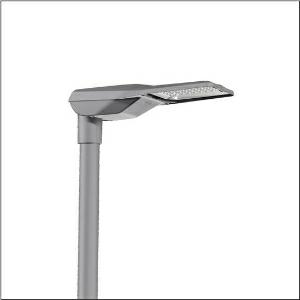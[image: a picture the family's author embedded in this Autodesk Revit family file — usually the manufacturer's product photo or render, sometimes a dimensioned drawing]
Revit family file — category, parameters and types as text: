
# Revit family: streetlight_sl_21_iq_mini___st0_5a_5xe2b41g08jb_20f7
name_source: partatom
category: Lighting Fixtures
units: mm (PartAtom-declared; Revit-internal decimal feet)

## family parameters
Cut with Voids When Loaded = No
Host = Face
Light Source = No
Part Type = Normal
Room Calculation Point = No
Round Connector Dimension = Use Diameter
Shared = No

## types (1)
- --- (1 x LED, 11290 lm, 71.6 W, 4000K)
    Apparent Load = 72 VA
    CIE Flux Codes = 43 76 97 100 100
    Color Rendering = 70
    Color Temperature = 4000K
    Default Elevation = 1800 mm
    Description = Streetlight SL 21 iQ mini, mast luminaire, primary light control with lens, of PMMA, primary optical cover: cover, of toughened safety glass, transparent, light distribution: ST0.5a, light emission: direct distribution, primary light characteristic: asymmetric, installation type: post-top, side-entry, LED, High Power LED, rated luminous flux: 11.290lm, luminous efficacy: 158lm/W, light colour: 740, colour temperature: 4000K, control gear: iQ Street-Remote, control: Street-Remote, Auto-Match, Temp-Guard, Lumen-Switch, Night-Set, Smart-Wire, Light-Fading, Desk-Remote (wireless, voltage-free reading and setting of iQ features in the workshop via application-optimized NFC function/RFID function), optimised constant luminous flux control (CLO 2.0), pre-setting: linear dimming characteristic, mains connection: 220..240V, AC, 50/60Hz, start of lifetime: 72W, end of service life: 75W, reduction: 33W, luminaire housing, of diecast aluminium, powder-coated, SITECO metallic grey (DB 702S), corrosivity category C5 high according to DIN EN ISO 12944, please order mast flange separately, inclination adjustable: 0°, 5°, 10°, 15°, sealing non-destructively replaceable, multi-level sealing system, length: 628mm, width: 235mm, height: 110mm, mast flange for spigot size: 42mm (side-entry): 5XC10008XM4, 60/48mm (side-entry/post-top): 5XC10108XM2, 76/60mm (side-entry/post-top): 5XC10108XM1, mounting height: 4..8m, protection rating (complete): IP66, insulation class (complete): insulation class II (safety insulation), certification: CE, ENEC, ENEC+, VDE, impact resistance: IK10, permissible operating ambient temperature for outdoor applications: -40..+50°C, standard-compliant lighting for roads and squares, packaging unit: 1 piece

Light Distribution: ST0.5a
    Height = 110 mm
    Lamp = 1 x LED
    Lamp Light Flux = 11290 lm
    Lamp Power = 71.6 W
    Lamp count = 1
    Length = 625 mm
    Luminous efficacy = 158 lm/W
    Manufacturer = Siteco
    ModVariant = No
    Model = 5XE2B41G08JB
    Number of Poles = 1
    OnlyDefault = Yes
    Power Factor = 1
    Product Name = Streetlight SL 21 iQ mini | ST0.5a
    Product group = mast luminaire | pylon top
    ProductGroupID = 6100
    Protection Class = Protection class II
    Protection Degree = IP 66
    RLX_Detail_Level = 1
    RLX_Emergency_Light_Flux = 0 lm
    RLX_Emergency_Type = 0
    RLX_Emergency_Type_DB = No
    RlxData = <blob elided: 37489 chars, md5=e32aa042>
    Socket = socket
    Standby Power = 0 W
    System Light Flux = 11290 lm
    System Power = 72 W
    Type Comments = factory setting: luminous flux: 100 % | dim-lin: 254 | 746 mA
    Type Image = l_1003519.jpg
    URL = http://relux.com
    VarID = @adj_171179
    Voltage = 0 V
    Weight = 0.00 kg
    Width = 234 mm

## geometry (parser evidence)
native form markers: Blend x4, Sweep x12
no freeform markers — native parametric forms only
